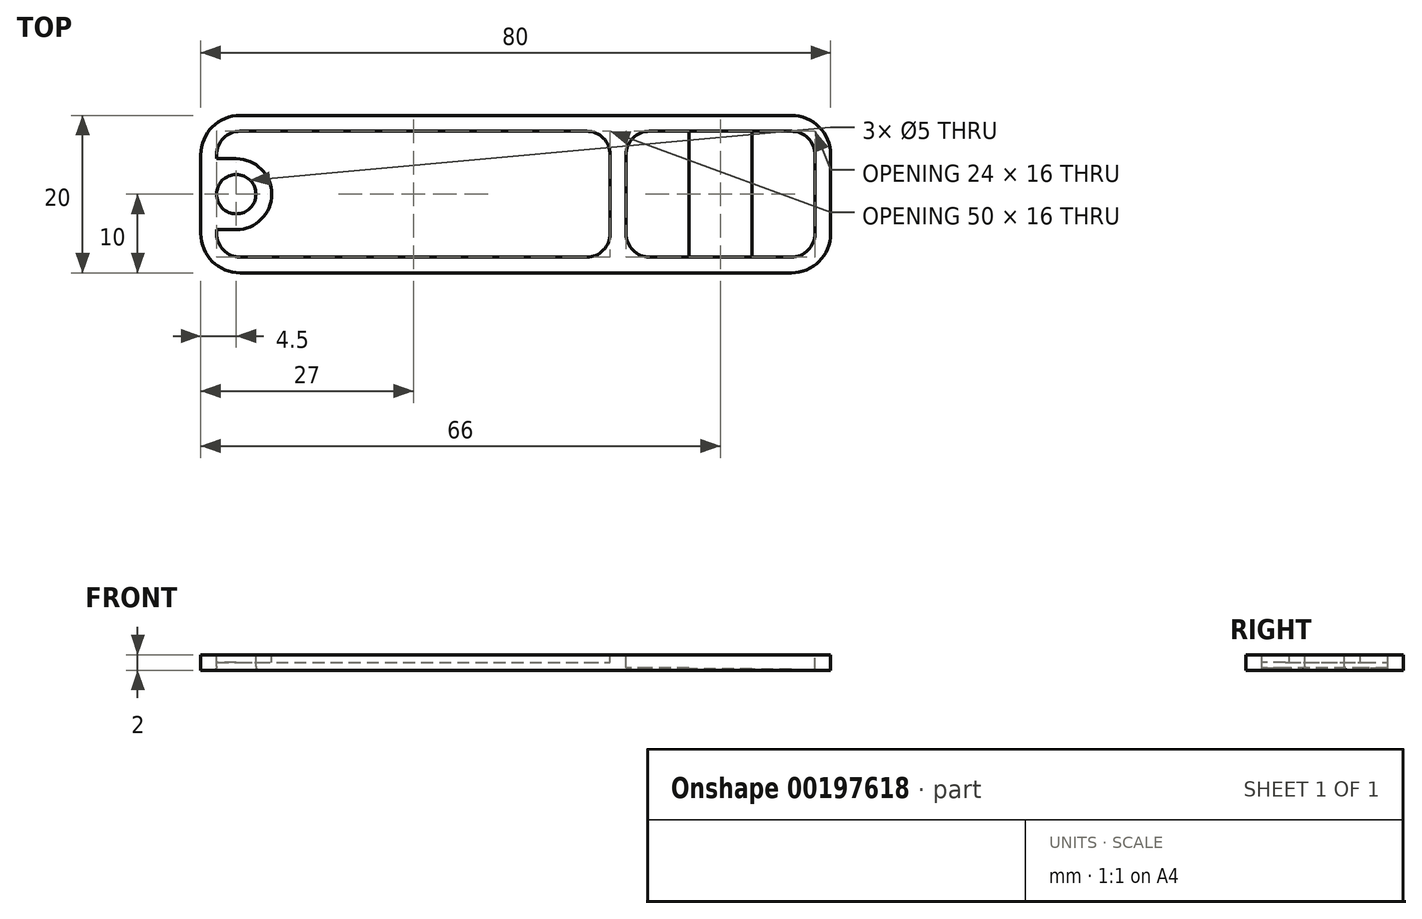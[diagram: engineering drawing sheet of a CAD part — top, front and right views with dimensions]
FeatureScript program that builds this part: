
annotation { "Feature Type Name" : "Feature", "Feature Type Description" : "" }
export const myFeature = defineFeature(function(context is Context, id is Id, definition is map)
    precondition{}
    {
        {
            var Q0;
            Q0=qCreatedBy(makeId("Top.planeOp"),FACE);
            var sketch = newSketch(context, id + "F0", { "sketchPlane" : qUnion([Q0])});
            skLineSegment(sketch, "E0.bottom", {"start": v(35, 10) * mm, "end": v(-35, 10) * mm});
            skLineSegment(sketch, "E0.top", {"start": v(35, -10) * mm, "end": v(-35, -10) * mm});
            skLineSegment(sketch, "E0.left", {"start": v(40, 5) * mm, "end": v(40, -5) * mm});
            skLineSegment(sketch, "E0.right", {"start": v(-40, 5) * mm, "end": v(-40, -5) * mm});
            skPoint(sketch, "E0.middle", {"position": v(0, 0) * mm});
            skPoint(sketch, "E1.visualSharp", {"position": v(-40, 10) * mm});
            skArc(sketch, "E1.filletArc", {"start": v(-35, 10) * mm, "mid": v(-38.54, 8.54) * mm, "end": v(-40, 5) * mm});
            skPoint(sketch, "E2.visualSharp", {"position": v(40, 10) * mm});
            skArc(sketch, "E2.filletArc", {"start": v(40, 5) * mm, "mid": v(38.54, 8.54) * mm, "end": v(35, 10) * mm});
            skPoint(sketch, "E3.visualSharp", {"position": v(40, -10) * mm});
            skArc(sketch, "E3.filletArc", {"start": v(35, -10) * mm, "mid": v(38.54, -8.54) * mm, "end": v(40, -5) * mm});
            skPoint(sketch, "E4.visualSharp", {"position": v(-40, -10) * mm});
            skArc(sketch, "E4.filletArc", {"start": v(-40, -5) * mm, "mid": v(-38.54, -8.54) * mm, "end": v(-35, -10) * mm});
            skSolve(sketch);
        }
        {
            var Q0;
            Q0 = qSketchRegion(id + "F0", true);
            extrude(context, id + "F1", {"entities" : qUnion([Q0]), "depth" : 2 * mm});
        }
        {
            var Q0;
            Q0=makeQuery(id+"F1.opExtrude","CAP_FACE",FACE,{"disambiguationData":[OSD([sQuery(id+"F0.wireOp",EDGE,"E0.bottom"),sQuery(id+"F0.wireOp",EDGE,"E0.top"),sQuery(id+"F0.wireOp",EDGE,"E0.left"),sQuery(id+"F0.wireOp",EDGE,"E0.right"),sQuery(id+"F0.wireOp",EDGE,"E1.filletArc"),sQuery(id+"F0.wireOp",EDGE,"E2.filletArc"),sQuery(id+"F0.wireOp",EDGE,"E3.filletArc"),sQuery(id+"F0.wireOp",EDGE,"E4.filletArc")])],"isStart":false});
            var sketch = newSketch(context, id + "F2", { "sketchPlane" : qUnion([Q0])});
            skLineSegment(sketch, "E5.0", {"start": v(38, -5) * mm, "end": v(38, 5) * mm});
            skArc(sketch, "E5.1", {"start": v(35, -8) * mm, "mid": v(37.12, -7.12) * mm, "end": v(38, -5) * mm});
            skArc(sketch, "E5.2", {"start": v(38, 5) * mm, "mid": v(37.12, 7.12) * mm, "end": v(35, 8) * mm});
            skLineSegment(sketch, "E5.3", {"start": v(-35, -8) * mm, "end": v(9, -8) * mm});
            skLineSegment(sketch, "E5.4", {"start": v(35, 8) * mm, "end": v(17, 8) * mm});
            skArc(sketch, "E5.5", {"start": v(-35, 8) * mm, "mid": v(-37.12, 7.12) * mm, "end": v(-38, 5) * mm});
            skArc(sketch, "E5.7", {"start": v(-38, -5) * mm, "mid": v(-37.12, -7.12) * mm, "end": v(-35, -8) * mm});
            skCircle(sketch, "E6", {"center": v(-35.5, 0) * mm, "radius": 2.5 * mm, "construction": true});
            skArc(sketch, "E7.0", {"start": v(-35.5, -4.5) * mm, "mid": v(-31, 0) * mm, "end": v(-35.5, 4.5) * mm});
            skLineSegment(sketch, "E8", {"start": v(-38, -5) * mm, "end": v(-38, -4.5) * mm});
            skLineSegment(sketch, "E9", {"start": v(-35.5, 4.5) * mm, "end": v(-38, 4.5) * mm});
            skLineSegment(sketch, "E10", {"start": v(-35.5, -4.5) * mm, "end": v(-38, -4.5) * mm});
            skLineSegment(sketch, "E11.trimOffspring", {"start": v(-38, 4.5) * mm, "end": v(-38, 5) * mm});
            skArc(sketch, "E12", {"start": v(17, 8) * mm, "mid": v(14.88, 7.12) * mm, "end": v(14, 5) * mm});
            skArc(sketch, "E13", {"start": v(14, -5) * mm, "mid": v(14.88, -7.12) * mm, "end": v(17, -8) * mm});
            skLineSegment(sketch, "E14", {"start": v(14, -5) * mm, "end": v(14, 5) * mm});
            skArc(sketch, "E15", {"start": v(12, 5) * mm, "mid": v(11.12, 7.12) * mm, "end": v(9, 8) * mm});
            skArc(sketch, "E16", {"start": v(12, -5) * mm, "mid": v(11.12, -7.12) * mm, "end": v(9, -8) * mm});
            skLineSegment(sketch, "E17", {"start": v(12, -5) * mm, "end": v(12, 5) * mm});
            skLineSegment(sketch, "E18.trimOffspring", {"start": v(9, 8) * mm, "end": v(-35, 8) * mm});
            skLineSegment(sketch, "E19.trimOffspring", {"start": v(17, -8) * mm, "end": v(35, -8) * mm});
            skLineSegment(sketch, "E20", {"start": v(14, 0) * mm, "end": v(22, 0) * mm, "construction": true});
            skLineSegment(sketch, "E21", {"start": v(22, 0) * mm, "end": v(30, 0) * mm, "construction": true});
            skLineSegment(sketch, "E22", {"start": v(30, 0) * mm, "end": v(38, 0) * mm, "construction": true});
            skLineSegment(sketch, "E23", {"start": v(22, 8) * mm, "end": v(22, -8) * mm});
            skLineSegment(sketch, "E24", {"start": v(30, 8) * mm, "end": v(30, -8) * mm});
            skSolve(sketch);
        }
        {
            var Q0;
            Q0=makeQuery(id+"F2.imprint","IMPRINT",FACE,{"disambiguationData":[TD([[makeQuery(id+"F2.imprint","IMPRINT",EDGE,{"derivedFrom":sQuery(id+"F2.wireOp",EDGE,"E5.3")}),1.0]])]});
            extrude(context, id + "F3", {"entities" : qUnion([Q0]), "operationType" : NewBodyOperationType.REMOVE, "oppositeDirection" : true, "offsetDistance" : 25 * mm, "depth" : 1 * mm});
        }
        {
            var Q0;
            Q0=makeQuery(id+"F1.opExtrude","CAP_FACE",FACE,{"disambiguationData":[OSD([sQuery(id+"F0.wireOp",EDGE,"E0.bottom"),sQuery(id+"F0.wireOp",EDGE,"E0.top"),sQuery(id+"F0.wireOp",EDGE,"E0.left"),sQuery(id+"F0.wireOp",EDGE,"E0.right"),sQuery(id+"F0.wireOp",EDGE,"E1.filletArc"),sQuery(id+"F0.wireOp",EDGE,"E2.filletArc"),sQuery(id+"F0.wireOp",EDGE,"E3.filletArc"),sQuery(id+"F0.wireOp",EDGE,"E4.filletArc")])],"isStart":false});
            var sketch = newSketch(context, id + "F4", { "sketchPlane" : qUnion([Q0])});
            skCircle(sketch, "E25.0", {"center": v(-35.5, 0) * mm, "radius": 2.5 * mm});
            skSolve(sketch);
        }
        {
            var Q0;
            Q0 = qSketchRegion(id + "F4", true);
            extrude(context, id + "F5", {"entities" : qUnion([Q0]), "operationType" : NewBodyOperationType.REMOVE, "endBound" : BoundingType.THROUGH_ALL, "oppositeDirection" : true, "depth" : 25 * mm});
        }
        {
            var Q0;
            Q0=makeQuery(id+"F5.boolean.opBoolean","COPY",EDGE,{"derivedFrom":makeQuery(id+"F5.opExtrude","CAP_EDGE",EDGE,{"disambiguationData":[OSD([sQuery(id+"F4.wireOp",EDGE,"E25.0")])],"isStart":true})});
            var Q1;
            Q1=makeQuery(id+"F5.boolean.opBoolean","INTERSECT",EDGE,{"derivedFrom":[makeQuery(id+"F1.opExtrude","CAP_FACE",FACE,{"disambiguationData":[OSD([sQuery(id+"F0.wireOp",EDGE,"E0.bottom"),sQuery(id+"F0.wireOp",EDGE,"E0.top"),sQuery(id+"F0.wireOp",EDGE,"E0.left"),sQuery(id+"F0.wireOp",EDGE,"E0.right"),sQuery(id+"F0.wireOp",EDGE,"E1.filletArc"),sQuery(id+"F0.wireOp",EDGE,"E2.filletArc"),sQuery(id+"F0.wireOp",EDGE,"E3.filletArc"),sQuery(id+"F0.wireOp",EDGE,"E4.filletArc")])],"isStart":true}),makeQuery(id+"F5.opExtrude","SWEPT_FACE",FACE,{"disambiguationData":[OSD([sQuery(id+"F4.wireOp",EDGE,"E25.0")])]})]});
            fillet(context, id + "F6", {"entities" : qUnion([Q0, Q1]), "radius" : .5 * mm, "tangentPropagation" : true, "allowEdgeOverflow" : false});
        }
        {
            var Q0;
            Q0=makeQuery(id+"F1.opExtrude","SWEPT_BODY",BODY,{"disambiguationData":[OSD([sQuery(id+"F0.wireOp",EDGE,"E0.bottom"),sQuery(id+"F0.wireOp",EDGE,"E0.top"),sQuery(id+"F0.wireOp",EDGE,"E0.left"),sQuery(id+"F0.wireOp",EDGE,"E0.right"),sQuery(id+"F0.wireOp",EDGE,"E1.filletArc"),sQuery(id+"F0.wireOp",EDGE,"E2.filletArc"),sQuery(id+"F0.wireOp",EDGE,"E3.filletArc"),sQuery(id+"F0.wireOp",EDGE,"E4.filletArc")])]});
            transform(context, id + "F7", {"entities" : qUnion([Q0]), "transformType" : TransformType.COPY});
        }
        {
            var Q0;
            Q0=makeQuery(id+"F1.opExtrude","SWEPT_BODY",BODY,{"disambiguationData":[OSD([sQuery(id+"F0.wireOp",EDGE,"E0.bottom"),sQuery(id+"F0.wireOp",EDGE,"E0.top"),sQuery(id+"F0.wireOp",EDGE,"E0.left"),sQuery(id+"F0.wireOp",EDGE,"E0.right"),sQuery(id+"F0.wireOp",EDGE,"E1.filletArc"),sQuery(id+"F0.wireOp",EDGE,"E2.filletArc"),sQuery(id+"F0.wireOp",EDGE,"E3.filletArc"),sQuery(id+"F0.wireOp",EDGE,"E4.filletArc")])]});
            transform(context, id + "F8", {"entities" : qUnion([Q0]), "transformType" : TransformType.COPY});
        }
        {
            var Q0;
            {var subQ1=sQuery(id+"F2.wireOp",EDGE,"E12");Q0=makeQuery(id+"F2.imprint","IMPRINT",FACE,{"disambiguationData":[TD([[makeQuery(id+"F2.imprint","IMPRINT",EDGE,{"derivedFrom":subQ1}),1.0]])]});}
            var Q1;
            Q1=makeQuery(id+"F1.opExtrude","CAP_FACE",FACE,{"disambiguationData":[OSD([sQuery(id+"F0.wireOp",EDGE,"E0.bottom"),sQuery(id+"F0.wireOp",EDGE,"E0.top"),sQuery(id+"F0.wireOp",EDGE,"E0.left"),sQuery(id+"F0.wireOp",EDGE,"E0.right"),sQuery(id+"F0.wireOp",EDGE,"E1.filletArc"),sQuery(id+"F0.wireOp",EDGE,"E2.filletArc"),sQuery(id+"F0.wireOp",EDGE,"E3.filletArc"),sQuery(id+"F0.wireOp",EDGE,"E4.filletArc")])],"isStart":true});
            extrude(context, id + "F9", {"entities" : qUnion([Q0]), "operationType" : NewBodyOperationType.REMOVE, "endBound" : BoundingType.UP_TO_SURFACE, "oppositeDirection" : true, "endBoundEntityFace" : qUnion([Q1]), "hasOffset" : true, "offsetDistance" : 0.3 * mm, "depth" : 0.7 * mm});
        }
        {
            var Q0;
            {var subQ0=sQuery(id+"F2.wireOp",EDGE,"E23");Q0=makeQuery(id+"F2.imprint","IMPRINT",FACE,{"disambiguationData":[TD([[makeQuery(id+"F2.imprint","IMPRINT",EDGE,{"derivedFrom":subQ0}),1.0]])]});}
            var Q1;
            Q1=makeQuery(id+"F1.opExtrude","CAP_FACE",FACE,{"disambiguationData":[OSD([sQuery(id+"F0.wireOp",EDGE,"E0.bottom"),sQuery(id+"F0.wireOp",EDGE,"E0.top"),sQuery(id+"F0.wireOp",EDGE,"E0.left"),sQuery(id+"F0.wireOp",EDGE,"E0.right"),sQuery(id+"F0.wireOp",EDGE,"E1.filletArc"),sQuery(id+"F0.wireOp",EDGE,"E2.filletArc"),sQuery(id+"F0.wireOp",EDGE,"E3.filletArc"),sQuery(id+"F0.wireOp",EDGE,"E4.filletArc")])],"isStart":true});
            extrude(context, id + "F10", {"entities" : qUnion([Q0]), "operationType" : NewBodyOperationType.REMOVE, "endBound" : BoundingType.UP_TO_SURFACE, "oppositeDirection" : true, "endBoundEntityFace" : qUnion([Q1]), "hasOffset" : true, "offsetDistance" : 0.2 * mm, "depth" : 0.1 * mm});
        }
        {
            var Q0;
            Q0=makeQuery(id+"F2.imprint","IMPRINT",FACE,{"disambiguationData":[TD([[makeQuery(id+"F2.imprint","IMPRINT",EDGE,{"derivedFrom":sQuery(id+"F2.wireOp",EDGE,"E5.0")}),1.0]])]});
            var Q1;
            Q1=makeQuery(id+"F1.opExtrude","CAP_FACE",FACE,{"disambiguationData":[OSD([sQuery(id+"F0.wireOp",EDGE,"E0.bottom"),sQuery(id+"F0.wireOp",EDGE,"E0.top"),sQuery(id+"F0.wireOp",EDGE,"E0.left"),sQuery(id+"F0.wireOp",EDGE,"E0.right"),sQuery(id+"F0.wireOp",EDGE,"E1.filletArc"),sQuery(id+"F0.wireOp",EDGE,"E2.filletArc"),sQuery(id+"F0.wireOp",EDGE,"E3.filletArc"),sQuery(id+"F0.wireOp",EDGE,"E4.filletArc")])],"isStart":true});
            extrude(context, id + "F11", {"entities" : qUnion([Q0]), "operationType" : NewBodyOperationType.REMOVE, "endBound" : BoundingType.UP_TO_SURFACE, "oppositeDirection" : true, "endBoundEntityFace" : qUnion([Q1]), "hasOffset" : true, "offsetDistance" : 0.1 * mm, "depth" : 0.1 * mm});
        }
        {
            var Q0;
            {var subQ1=sQuery(id+"F2.wireOp",EDGE,"E12");Q0=makeQuery(id+"F2.imprint","IMPRINT",FACE,{"disambiguationData":[TD([[makeQuery(id+"F2.imprint","IMPRINT",EDGE,{"derivedFrom":subQ1}),1.0]])]});}
            var Q1;
            Q1=makeQuery(id+"F1.opExtrude","CAP_FACE",FACE,{"disambiguationData":[OSD([sQuery(id+"F0.wireOp",EDGE,"E0.bottom"),sQuery(id+"F0.wireOp",EDGE,"E0.top"),sQuery(id+"F0.wireOp",EDGE,"E0.left"),sQuery(id+"F0.wireOp",EDGE,"E0.right"),sQuery(id+"F0.wireOp",EDGE,"E1.filletArc"),sQuery(id+"F0.wireOp",EDGE,"E2.filletArc"),sQuery(id+"F0.wireOp",EDGE,"E3.filletArc"),sQuery(id+"F0.wireOp",EDGE,"E4.filletArc")])],"isStart":true});
            extrude(context, id + "F12", {"entities" : qUnion([Q0]), "operationType" : NewBodyOperationType.REMOVE, "endBound" : BoundingType.UP_TO_SURFACE, "oppositeDirection" : true, "depth" : 25 * mm, "endBoundEntityFace" : qUnion([Q1]), "hasOffset" : true, "offsetDistance" : 1.2 * mm});
        }
        {
            var Q0;
            {var subQ0=sQuery(id+"F2.wireOp",EDGE,"E23");Q0=makeQuery(id+"F2.imprint","IMPRINT",FACE,{"disambiguationData":[TD([[makeQuery(id+"F2.imprint","IMPRINT",EDGE,{"derivedFrom":subQ0}),1.0]])]});}
            var Q1;
            Q1=makeQuery(id+"F7.opPattern","COPY",FACE,{"derivedFrom":makeQuery(id+"F1.opExtrude","CAP_FACE",FACE,{"disambiguationData":[OSD([sQuery(id+"F0.wireOp",EDGE,"E0.bottom"),sQuery(id+"F0.wireOp",EDGE,"E0.top"),sQuery(id+"F0.wireOp",EDGE,"E0.left"),sQuery(id+"F0.wireOp",EDGE,"E0.right"),sQuery(id+"F0.wireOp",EDGE,"E1.filletArc"),sQuery(id+"F0.wireOp",EDGE,"E2.filletArc"),sQuery(id+"F0.wireOp",EDGE,"E3.filletArc"),sQuery(id+"F0.wireOp",EDGE,"E4.filletArc")])],"isStart":true}),"instanceName":"1"});
            extrude(context, id + "F13", {"entities" : qUnion([Q0]), "operationType" : NewBodyOperationType.REMOVE, "endBound" : BoundingType.UP_TO_SURFACE, "oppositeDirection" : true, "depth" : 25 * mm, "endBoundEntityFace" : qUnion([Q1]), "hasOffset" : true, "offsetDistance" : 0.8 * mm});
        }
        {
            var Q0;
            Q0=makeQuery(id+"F2.imprint","IMPRINT",FACE,{"disambiguationData":[TD([[makeQuery(id+"F2.imprint","IMPRINT",EDGE,{"derivedFrom":sQuery(id+"F2.wireOp",EDGE,"E5.0")}),1.0]])]});
            var Q1;
            Q1=makeQuery(id+"F7.opPattern","COPY",FACE,{"derivedFrom":makeQuery(id+"F1.opExtrude","CAP_FACE",FACE,{"disambiguationData":[OSD([sQuery(id+"F0.wireOp",EDGE,"E0.bottom"),sQuery(id+"F0.wireOp",EDGE,"E0.top"),sQuery(id+"F0.wireOp",EDGE,"E0.left"),sQuery(id+"F0.wireOp",EDGE,"E0.right"),sQuery(id+"F0.wireOp",EDGE,"E1.filletArc"),sQuery(id+"F0.wireOp",EDGE,"E2.filletArc"),sQuery(id+"F0.wireOp",EDGE,"E3.filletArc"),sQuery(id+"F0.wireOp",EDGE,"E4.filletArc")])],"isStart":true}),"instanceName":"1"});
            extrude(context, id + "F14", {"entities" : qUnion([Q0]), "operationType" : NewBodyOperationType.REMOVE, "endBound" : BoundingType.UP_TO_SURFACE, "oppositeDirection" : true, "depth" : 25 * mm, "endBoundEntityFace" : qUnion([Q1]), "hasOffset" : true, "offsetDistance" : 0.4 * mm});
        }
        {
            var Q0;
            {var subQ1=sQuery(id+"F2.wireOp",EDGE,"E12");Q0=makeQuery(id+"F2.imprint","IMPRINT",FACE,{"disambiguationData":[TD([[makeQuery(id+"F2.imprint","IMPRINT",EDGE,{"derivedFrom":subQ1}),1.0]])]});}
            var Q1;
            Q1=makeQuery(id+"F7.opPattern","COPY",FACE,{"derivedFrom":makeQuery(id+"F1.opExtrude","CAP_FACE",FACE,{"disambiguationData":[OSD([sQuery(id+"F0.wireOp",EDGE,"E0.bottom"),sQuery(id+"F0.wireOp",EDGE,"E0.top"),sQuery(id+"F0.wireOp",EDGE,"E0.left"),sQuery(id+"F0.wireOp",EDGE,"E0.right"),sQuery(id+"F0.wireOp",EDGE,"E1.filletArc"),sQuery(id+"F0.wireOp",EDGE,"E2.filletArc"),sQuery(id+"F0.wireOp",EDGE,"E3.filletArc"),sQuery(id+"F0.wireOp",EDGE,"E4.filletArc")])],"isStart":true}),"instanceName":"1"});
            extrude(context, id + "F15", {"entities" : qUnion([Q0]), "operationType" : NewBodyOperationType.REMOVE, "endBound" : BoundingType.UP_TO_SURFACE, "oppositeDirection" : true, "depth" : 25 * mm, "endBoundEntityFace" : qUnion([Q1]), "hasOffset" : true, "offsetDistance" : 1.5 * mm});
        }
        {
            var Q0;
            {var subQ0=sQuery(id+"F2.wireOp",EDGE,"E23");Q0=makeQuery(id+"F2.imprint","IMPRINT",FACE,{"disambiguationData":[TD([[makeQuery(id+"F2.imprint","IMPRINT",EDGE,{"derivedFrom":subQ0}),1.0]])]});}
            var Q1;
            Q1=makeQuery(id+"F8.opPattern","COPY",FACE,{"derivedFrom":makeQuery(id+"F1.opExtrude","CAP_FACE",FACE,{"disambiguationData":[OSD([sQuery(id+"F0.wireOp",EDGE,"E0.bottom"),sQuery(id+"F0.wireOp",EDGE,"E0.top"),sQuery(id+"F0.wireOp",EDGE,"E0.left"),sQuery(id+"F0.wireOp",EDGE,"E0.right"),sQuery(id+"F0.wireOp",EDGE,"E1.filletArc"),sQuery(id+"F0.wireOp",EDGE,"E2.filletArc"),sQuery(id+"F0.wireOp",EDGE,"E3.filletArc"),sQuery(id+"F0.wireOp",EDGE,"E4.filletArc")])],"isStart":true}),"instanceName":"1"});
            extrude(context, id + "F16", {"entities" : qUnion([Q0]), "operationType" : NewBodyOperationType.REMOVE, "endBound" : BoundingType.UP_TO_SURFACE, "oppositeDirection" : true, "depth" : 25 * mm, "endBoundEntityFace" : qUnion([Q1]), "hasOffset" : true, "offsetDistance" : 1 * mm});
        }
        {
            var Q0;
            Q0=makeQuery(id+"F2.imprint","IMPRINT",FACE,{"disambiguationData":[TD([[makeQuery(id+"F2.imprint","IMPRINT",EDGE,{"derivedFrom":sQuery(id+"F2.wireOp",EDGE,"E5.0")}),1.0]])]});
            var Q1;
            Q1=makeQuery(id+"F8.opPattern","COPY",FACE,{"derivedFrom":makeQuery(id+"F1.opExtrude","CAP_FACE",FACE,{"disambiguationData":[OSD([sQuery(id+"F0.wireOp",EDGE,"E0.bottom"),sQuery(id+"F0.wireOp",EDGE,"E0.top"),sQuery(id+"F0.wireOp",EDGE,"E0.left"),sQuery(id+"F0.wireOp",EDGE,"E0.right"),sQuery(id+"F0.wireOp",EDGE,"E1.filletArc"),sQuery(id+"F0.wireOp",EDGE,"E2.filletArc"),sQuery(id+"F0.wireOp",EDGE,"E3.filletArc"),sQuery(id+"F0.wireOp",EDGE,"E4.filletArc")])],"isStart":true}),"instanceName":"1"});
            extrude(context, id + "F17", {"entities" : qUnion([Q0]), "operationType" : NewBodyOperationType.REMOVE, "endBound" : BoundingType.UP_TO_SURFACE, "oppositeDirection" : true, "depth" : 25 * mm, "endBoundEntityFace" : qUnion([Q1]), "hasOffset" : true, "offsetDistance" : 0.5 * mm});
        }
    });
